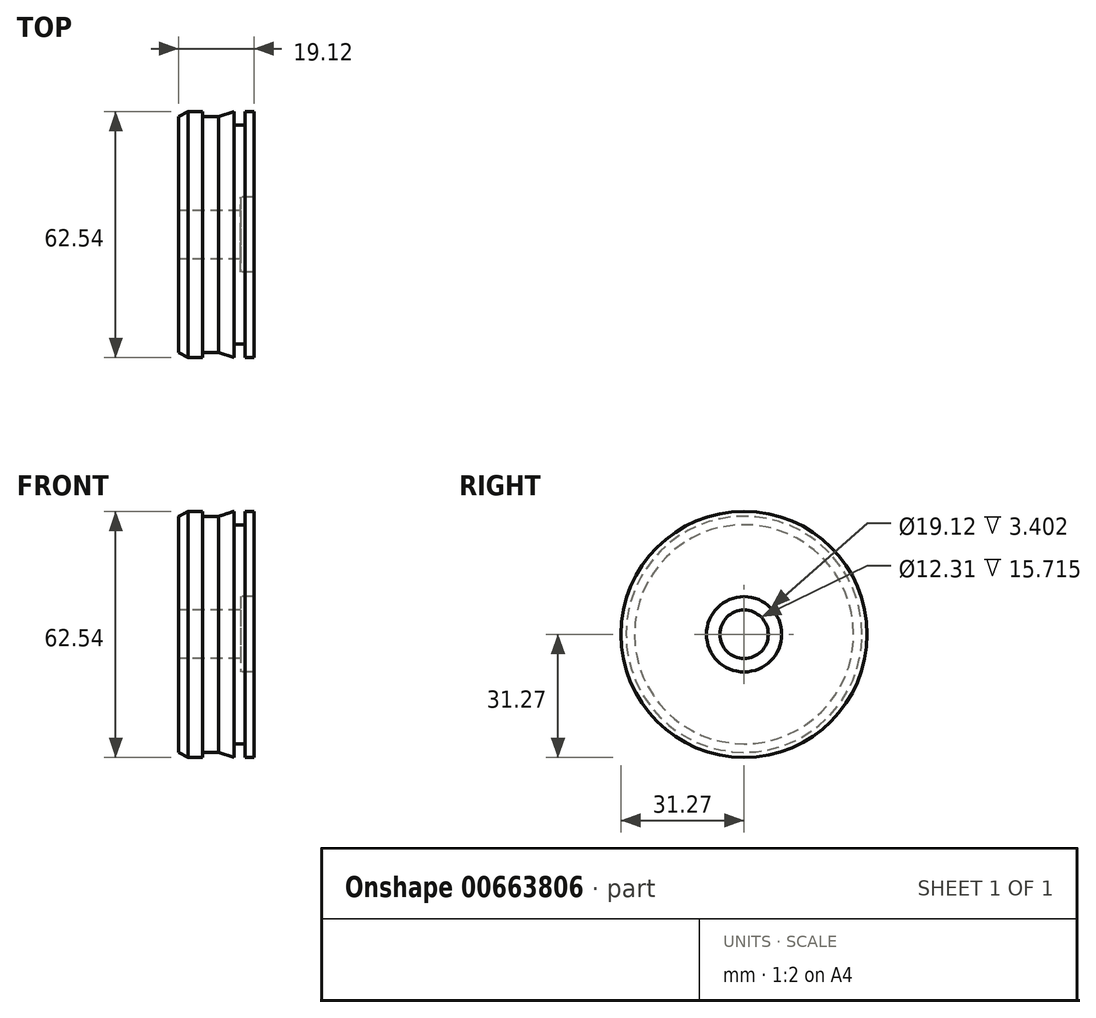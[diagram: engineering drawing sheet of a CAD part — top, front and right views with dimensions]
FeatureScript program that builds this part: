
annotation { "Feature Type Name" : "Feature", "Feature Type Description" : "" }
export const myFeature = defineFeature(function(context is Context, id is Id, definition is map)
    precondition{}
    {
        {
            var Q0;
            Q0=qCreatedBy(makeId("Front.planeOp"),FACE);
            var sketch = newSketch(context, id + "F0", { "sketchPlane" : qUnion([Q0])});
            skLineSegment(sketch, "E0", {"start": v(0, 9.56) * mm, "end": v(0, 31.27) * mm});
            skLineSegment(sketch, "E1", {"start": v(0, 31.27) * mm, "end": v(-2.27, 31.27) * mm});
            skLineSegment(sketch, "E2", {"start": v(-2.27, 31.27) * mm, "end": v(-2.27, 27.83) * mm});
            skLineSegment(sketch, "E3", {"start": v(-2.27, 27.83) * mm, "end": v(-5.05, 27.83) * mm});
            skLineSegment(sketch, "E4", {"start": v(-5.05, 27.83) * mm, "end": v(-5.05, 31.27) * mm});
            skLineSegment(sketch, "E5", {"start": v(-5.05, 31.27) * mm, "end": v(-8.94, 29.97) * mm});
            skLineSegment(sketch, "E6", {"start": v(-8.94, 29.97) * mm, "end": v(-13.12, 29.97) * mm});
            skLineSegment(sketch, "E7", {"start": v(-13.12, 29.97) * mm, "end": v(-13.12, 31.27) * mm});
            skLineSegment(sketch, "E8", {"start": v(-13.12, 31.27) * mm, "end": v(-16.69, 31.27) * mm});
            skLineSegment(sketch, "E9", {"start": v(-16.69, 31.27) * mm, "end": v(-19.12, 29.97) * mm});
            skLineSegment(sketch, "E10", {"start": v(-19.12, 29.97) * mm, "end": v(-19.12, 9.56) * mm});
            skLineSegment(sketch, "E11", {"start": v(-19.12, 9.56) * mm, "end": v(-19.12, 6.16) * mm});
            skLineSegment(sketch, "E12", {"start": v(-19.12, 6.16) * mm, "end": v(-3.4, 6.16) * mm});
            skLineSegment(sketch, "E13", {"start": v(-3.4, 6.16) * mm, "end": v(-3.4, 9.56) * mm});
            skLineSegment(sketch, "E14", {"start": v(-3.4, 9.56) * mm, "end": v(0, 9.56) * mm});
            skLineSegment(sketch, "E15", {"start": v(-31.92, 0) * mm, "end": v(8.42, 0) * mm});
            skSolve(sketch);
        }
        {
            var Q0;
            Q0=makeQuery(id+"F0.imprint","IMPRINT",FACE,{"disambiguationData":[TD([[makeQuery(id+"F0.imprint","IMPRINT",EDGE,{"derivedFrom":sQuery(id+"F0.wireOp",EDGE,"E0")}),1.0]])]});
            var Q1;
            Q1=sQuery(id+"F0.wireOp",EDGE,"E15");
            revolve(context, id + "F1", {"entities" : qUnion([Q0]), "axis" : qUnion([Q1]), "revolveType" : RevolveType.FULL});
        }
    });
